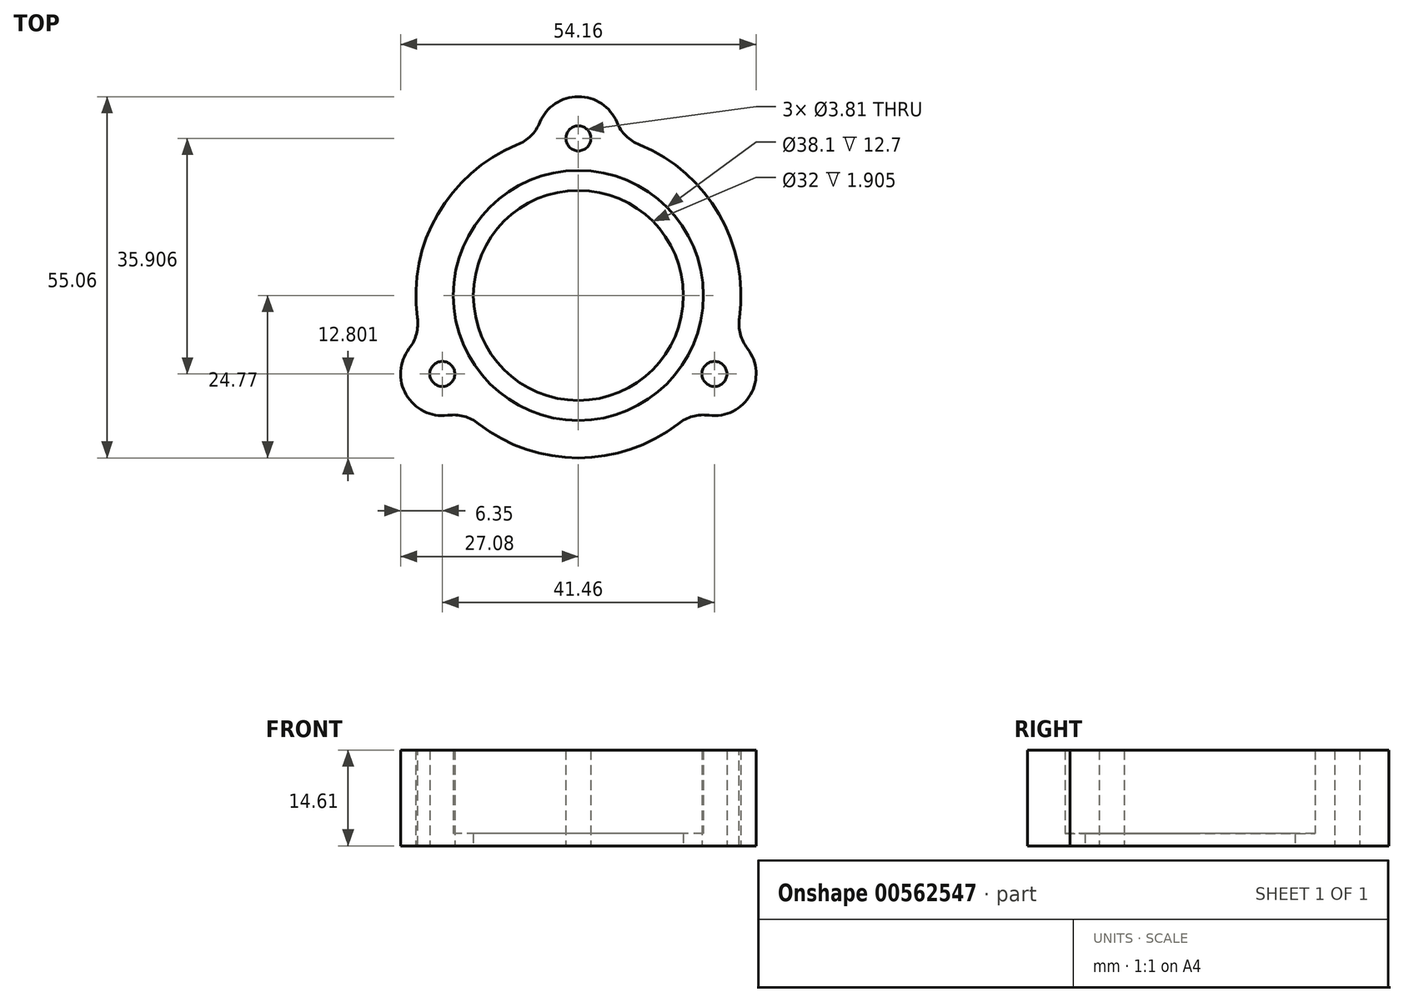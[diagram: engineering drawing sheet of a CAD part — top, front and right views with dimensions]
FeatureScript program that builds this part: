
annotation { "Feature Type Name" : "Feature", "Feature Type Description" : "" }
export const myFeature = defineFeature(function(context is Context, id is Id, definition is map)
    precondition{}
    {
        {
            var Q0;
            Q0=qCreatedBy(makeId("Top.planeOp"),FACE);
            var sketch = newSketch(context, id + "F0", { "sketchPlane" : qUnion([Q0])});
            skCircle(sketch, "E0", {"center": v(0.43, 0.63) * mm, "radius": 19.05 * mm});
            skCircle(sketch, "E1", {"center": v(0.43, 0.63) * mm, "radius": 24.77 * mm});
            skLineSegment(sketch, "E2", {"start": v(0.43, 0.63) * mm, "end": v(0.43, 43.4) * mm, "construction": true});
            skLineSegment(sketch, "E3", {"start": v(0.43, 0.63) * mm, "end": v(-43.28, -24.6) * mm, "construction": true});
            skLineSegment(sketch, "E4", {"start": v(0.43, 0.63) * mm, "end": v(47.33, -26.45) * mm, "construction": true});
            skLineSegment(sketch, "E5", {"start": v(-5.92, 2.79) * mm, "end": v(-5.92, 49.6) * mm, "construction": true});
            skLineSegment(sketch, "E6.MirrorCS", {"start": v(6.78, 2.79) * mm, "end": v(6.78, 49.6) * mm, "construction": true});
            skLineSegment(sketch, "E7", {"start": v(-10.8, 1.48) * mm, "end": v(-48.56, -20.32) * mm, "construction": true});
            skLineSegment(sketch, "E8.MirrorCS", {"start": v(-4.45, -9.52) * mm, "end": v(-42.2, -31.32) * mm, "construction": true});
            skLineSegment(sketch, "E9", {"start": v(0.57, -6.78) * mm, "end": v(38.9, -28.92) * mm, "construction": true});
            skLineSegment(sketch, "E10.MirrorCS", {"start": v(6.92, 4.22) * mm, "end": v(45.26, -17.92) * mm, "construction": true});
            skArc(sketch, "E11", {"start": v(6.78, 24.57) * mm, "mid": v(0.43, 30.92) * mm, "end": v(-5.92, 24.57) * mm});
            skArc(sketch, "E12", {"start": v(-23.48, -5.84) * mm, "mid": v(-25.8, -14.51) * mm, "end": v(-17.13, -16.84) * mm});
            skArc(sketch, "E13", {"start": v(17.99, -16.84) * mm, "mid": v(26.66, -14.51) * mm, "end": v(24.34, -5.84) * mm});
            skCircle(sketch, "E14", {"center": v(0.43, 24.57) * mm, "radius": 1.9 * mm});
            skCircle(sketch, "E15", {"center": v(-20.3, -11.34) * mm, "radius": 1.9 * mm});
            skCircle(sketch, "E16", {"center": v(21.16, -11.34) * mm, "radius": 1.9 * mm});
            skCircle(sketch, "E17", {"center": v(0.43, 0.63) * mm, "radius": 16 * mm});
            skSolve(sketch);
        }
        {
            var Q0;
            Q0=makeQuery(id+"F0.imprint","IMPRINT",FACE,{"disambiguationData":[TD([[makeQuery(id+"F0.imprint","IMPRINT",EDGE,{"derivedFrom":sQuery(id+"F0.wireOp",EDGE,"E0")}),-1.0]])]});
            var Q1;
            {var subQ0=sQuery(id+"F0.wireOp",EDGE,"E12");Q1=makeQuery(id+"F0.imprint","IMPRINT",FACE,{"disambiguationData":[TD([[makeQuery(id+"F0.imprint","IMPRINT",EDGE,{"derivedFrom":subQ0}),1.0]])]});}
            var Q2;
            {var subQ0=sQuery(id+"F0.wireOp",EDGE,"E13");Q2=makeQuery(id+"F0.imprint","IMPRINT",FACE,{"disambiguationData":[TD([[makeQuery(id+"F0.imprint","IMPRINT",EDGE,{"derivedFrom":subQ0}),1.0]])]});}
            var Q3;
            {var subQ0=sQuery(id+"F0.wireOp",EDGE,"E11");Q3=makeQuery(id+"F0.imprint","IMPRINT",FACE,{"disambiguationData":[TD([[makeQuery(id+"F0.imprint","IMPRINT",EDGE,{"derivedFrom":subQ0}),1.0]])]});}
            extrude(context, id + "F1", {"entities" : qUnion([Q0, Q1, Q2, Q3]), "depth" : 14.6 * mm, "offsetDistance" : 25.4 * mm});
        }
        {
            var Q0;
            Q0=makeQuery(id+"F0.imprint","IMPRINT",FACE,{"disambiguationData":[TD([[makeQuery(id+"F0.imprint","IMPRINT",EDGE,{"derivedFrom":sQuery(id+"F0.wireOp",EDGE,"E0")}),1.0]])]});
            extrude(context, id + "F2", {"entities" : qUnion([Q0]), "operationType" : NewBodyOperationType.ADD, "depth" : 1.9 * mm, "offsetDistance" : 25.4 * mm});
        }
        {
            var Q0;
            {var subQ0=sQuery(id+"F0.wireOp",EDGE,"E13");var subQ1=sQuery(id+"F0.wireOp",EDGE,"E1");Q0=makeQuery(id+"F1.opExtrude","SWEPT_EDGE",EDGE,{"disambiguationData":[OSD([subQ1,subQ0]),TDD([makeQuery(id+"F0.imprint","INTERSECT",VERTEX,{"disambiguationData":[OD(1.0)],"derivedFrom":[subQ1,subQ0]})])]});}
            var Q1;
            {var subQ0=sQuery(id+"F0.wireOp",EDGE,"E13");var subQ1=sQuery(id+"F0.wireOp",EDGE,"E1");Q1=makeQuery(id+"F1.opExtrude","SWEPT_EDGE",EDGE,{"disambiguationData":[OSD([subQ1,subQ0]),TDD([makeQuery(id+"F0.imprint","INTERSECT",VERTEX,{"disambiguationData":[OD(0.0)],"derivedFrom":[subQ1,subQ0]})])]});}
            var Q2;
            {var subQ0=sQuery(id+"F0.wireOp",EDGE,"E12");var subQ1=sQuery(id+"F0.wireOp",EDGE,"E1");Q2=makeQuery(id+"F1.opExtrude","SWEPT_EDGE",EDGE,{"disambiguationData":[OSD([subQ1,subQ0]),TDD([makeQuery(id+"F0.imprint","INTERSECT",VERTEX,{"disambiguationData":[OD(1.0)],"derivedFrom":[subQ1,subQ0]})])]});}
            var Q3;
            {var subQ0=sQuery(id+"F0.wireOp",EDGE,"E12");var subQ1=sQuery(id+"F0.wireOp",EDGE,"E1");Q3=makeQuery(id+"F1.opExtrude","SWEPT_EDGE",EDGE,{"disambiguationData":[OSD([subQ1,subQ0]),TDD([makeQuery(id+"F0.imprint","INTERSECT",VERTEX,{"disambiguationData":[OD(0.0)],"derivedFrom":[subQ1,subQ0]})])]});}
            var Q4;
            {var subQ0=sQuery(id+"F0.wireOp",EDGE,"E11");var subQ1=sQuery(id+"F0.wireOp",EDGE,"E1");Q4=makeQuery(id+"F1.opExtrude","SWEPT_EDGE",EDGE,{"disambiguationData":[OSD([subQ1,subQ0]),TDD([makeQuery(id+"F0.imprint","INTERSECT",VERTEX,{"disambiguationData":[OD(1.0)],"derivedFrom":[subQ1,subQ0]})])]});}
            var Q5;
            {var subQ0=sQuery(id+"F0.wireOp",EDGE,"E11");var subQ1=sQuery(id+"F0.wireOp",EDGE,"E1");Q5=makeQuery(id+"F1.opExtrude","SWEPT_EDGE",EDGE,{"disambiguationData":[OSD([subQ1,subQ0]),TDD([makeQuery(id+"F0.imprint","INTERSECT",VERTEX,{"disambiguationData":[OD(0.0)],"derivedFrom":[subQ1,subQ0]})])]});}
            fillet(context, id + "F3", {"entities" : qUnion([Q0, Q1, Q2, Q3, Q4, Q5]), "radius" : 6.35 * mm, "tangentPropagation" : true, "allowEdgeOverflow" : false});
        }
    });
